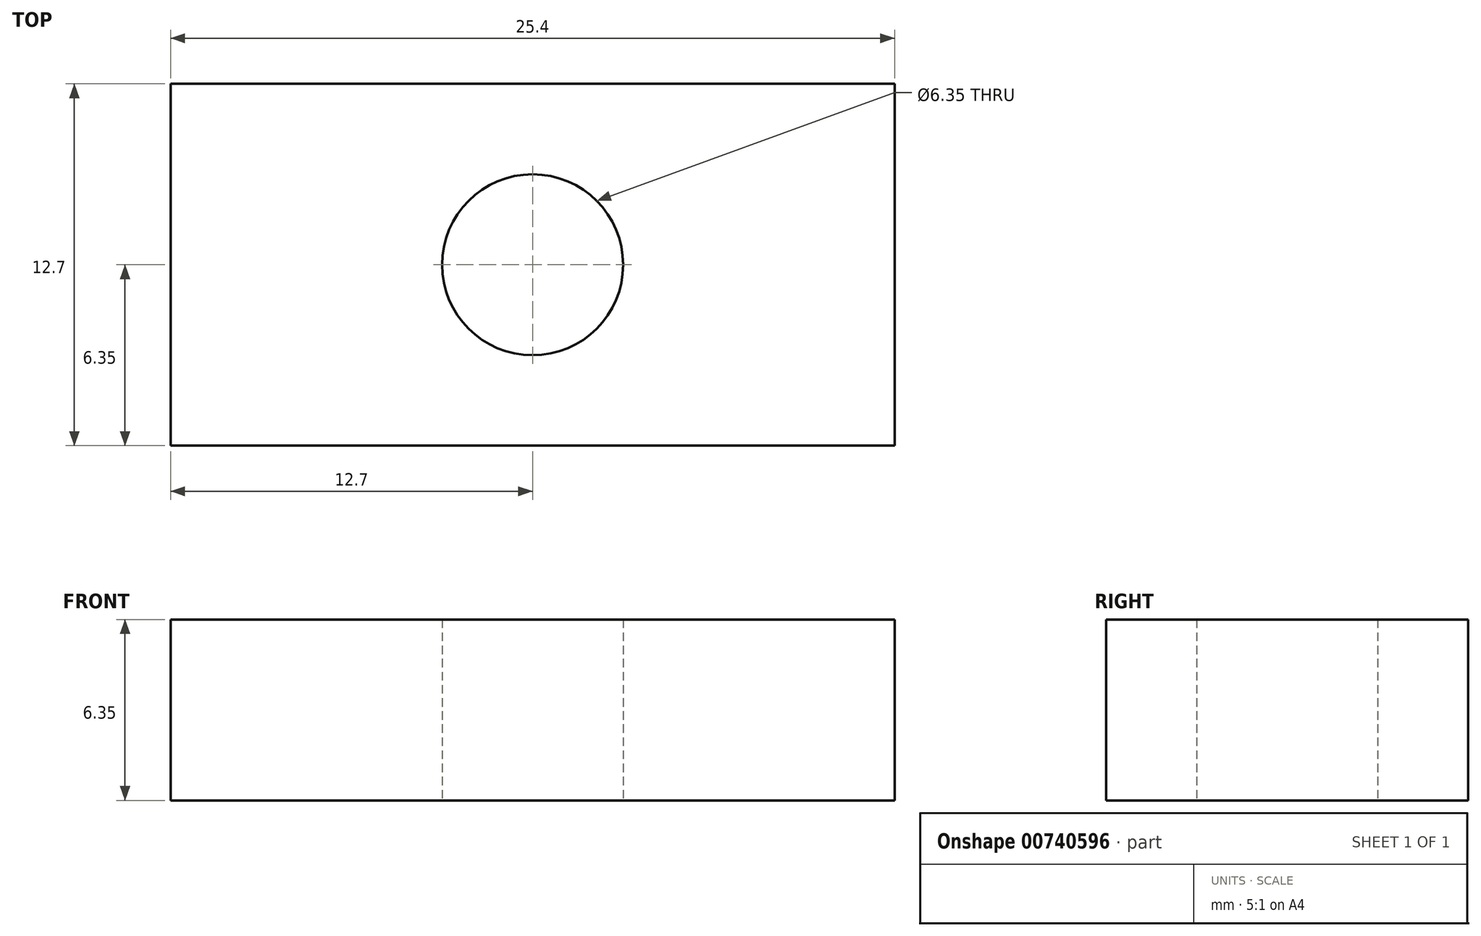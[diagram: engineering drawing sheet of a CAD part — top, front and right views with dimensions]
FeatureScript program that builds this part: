
annotation { "Feature Type Name" : "Feature", "Feature Type Description" : "" }
export const myFeature = defineFeature(function(context is Context, id is Id, definition is map)
    precondition{}
    {
        {
            var Q0;
            Q0=qCreatedBy(makeId("Top.planeOp"),FACE);
            var sketch = newSketch(context, id + "F0", { "sketchPlane" : qUnion([Q0])});
            skLineSegment(sketch, "E0.bottom", {"start": v(12.7, 6.35) * mm, "end": v(-12.7, 6.35) * mm});
            skLineSegment(sketch, "E0.top", {"start": v(12.7, -6.35) * mm, "end": v(-12.7, -6.35) * mm});
            skLineSegment(sketch, "E0.left", {"start": v(12.7, 6.35) * mm, "end": v(12.7, -6.35) * mm});
            skLineSegment(sketch, "E0.right", {"start": v(-12.7, 6.35) * mm, "end": v(-12.7, -6.35) * mm});
            skPoint(sketch, "E0.middle", {"position": v(0, 0) * mm});
            skCircle(sketch, "E1", {"center": v(0, 0) * mm, "radius": 3.18 * mm});
            skSolve(sketch);
        }
        {
            var Q0;
            Q0 = qSketchRegion(id + "F0", true);
            extrude(context, id + "F1", {"entities" : qUnion([Q0]), "depth" : 6.35 * mm, "offsetDistance" : 25.4 * mm});
        }
    });
